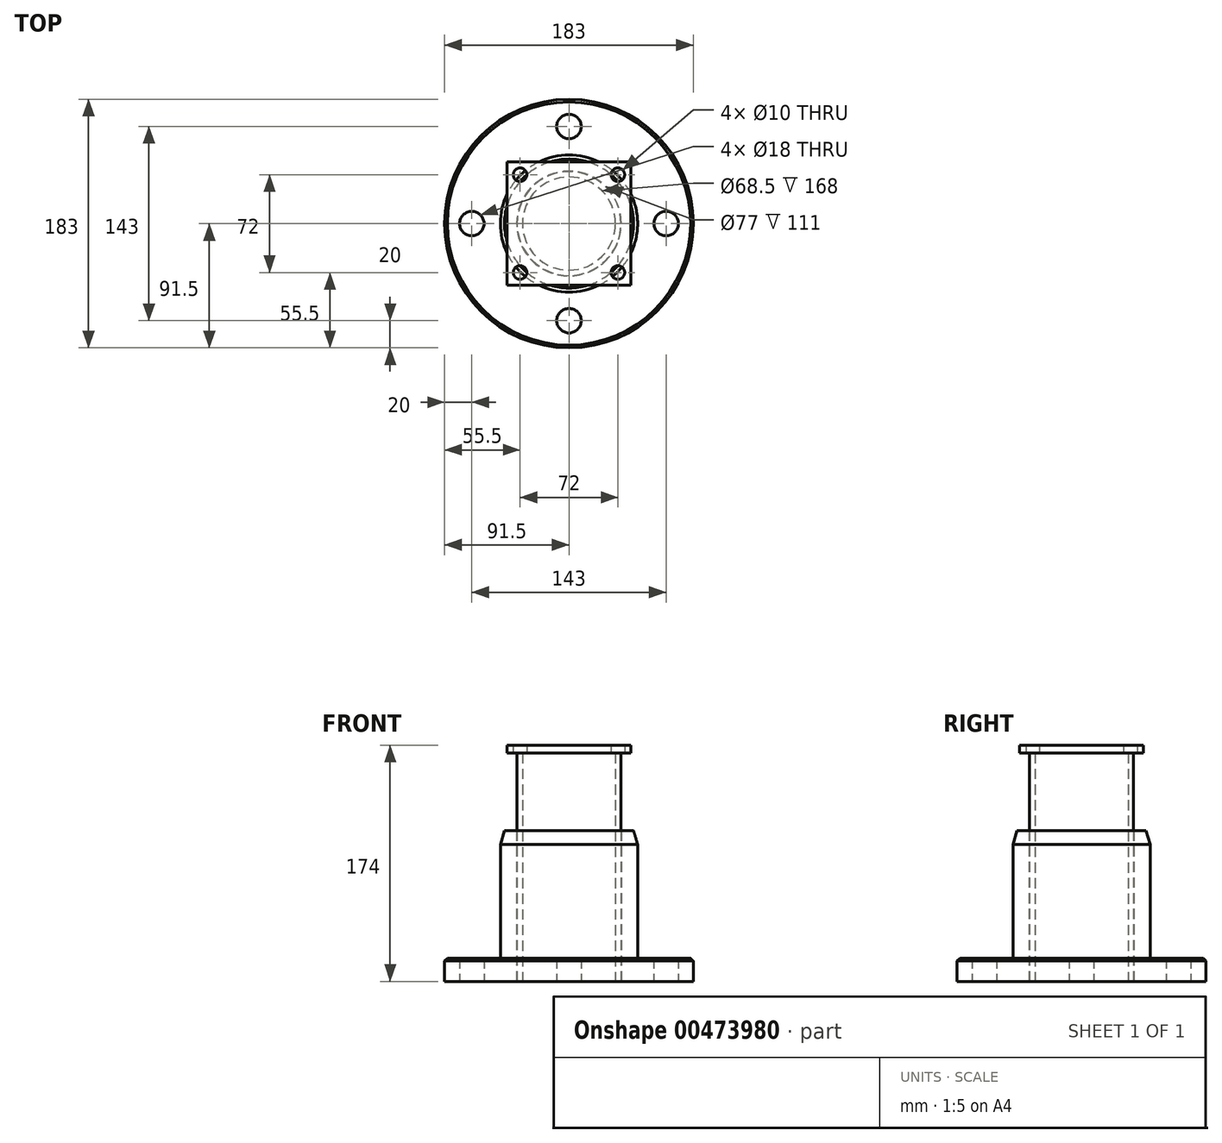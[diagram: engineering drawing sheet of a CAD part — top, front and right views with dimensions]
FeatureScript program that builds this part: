
annotation { "Feature Type Name" : "Feature", "Feature Type Description" : "" }
export const myFeature = defineFeature(function(context is Context, id is Id, definition is map)
    precondition{}
    {
        {
            var Q0;
            Q0=qCreatedBy(makeId("Top.planeOp"),FACE);
            var sketch = newSketch(context, id + "F0", { "sketchPlane" : qUnion([Q0])});
            skCircle(sketch, "E0", {"center": v(0, 0) * mm, "radius": 91.5 * mm});
            skCircle(sketch, "E1", {"center": v(0, 71.5) * mm, "radius": 9 * mm});
            skCircle(sketch, "E2", {"center": v(71.5, 0) * mm, "radius": 9 * mm});
            skCircle(sketch, "E3", {"center": v(-71.5, 0) * mm, "radius": 9 * mm});
            skCircle(sketch, "E4", {"center": v(0, -71.5) * mm, "radius": 9 * mm});
            skCircle(sketch, "E5", {"center": v(0, 0) * mm, "radius": 38.5 * mm});
            skCircle(sketch, "E6", {"center": v(0, 0) * mm, "radius": 71.5 * mm, "construction": true});
            skSolve(sketch);
        }
        {
            var Q0;
            Q0=makeQuery(id+"F0.imprint","IMPRINT",FACE,{"disambiguationData":[TD([[makeQuery(id+"F0.imprint","IMPRINT",EDGE,{"derivedFrom":sQuery(id+"F0.wireOp",EDGE,"E0")}),1.0]])]});
            extrude(context, id + "F1", {"entities" : qUnion([Q0]), "depth" : 17 * mm});
        }
        {
            var Q0;
            Q0=makeQuery(id+"F1.opExtrude","CAP_FACE",FACE,{"disambiguationData":[OSD([sQuery(id+"F0.wireOp",EDGE,"E0"),sQuery(id+"F0.wireOp",EDGE,"E1"),sQuery(id+"F0.wireOp",EDGE,"E2"),sQuery(id+"F0.wireOp",EDGE,"E3"),sQuery(id+"F0.wireOp",EDGE,"E4"),sQuery(id+"F0.wireOp",EDGE,"E5")])],"isStart":false});
            var sketch = newSketch(context, id + "F2", { "sketchPlane" : qUnion([Q0])});
            skCircle(sketch, "E7", {"center": v(0, 0) * mm, "radius": 50.5 * mm});
            skCircle(sketch, "E8", {"center": v(0, 0) * mm, "radius": 38.5 * mm});
            skSolve(sketch);
        }
        {
            var Q0;
            Q0=makeQuery(id+"F2.imprint","IMPRINT",FACE,{"disambiguationData":[TD([[makeQuery(id+"F2.imprint","IMPRINT",EDGE,{"derivedFrom":sQuery(id+"F2.wireOp",EDGE,"E7")}),1.0]])]});
            extrude(context, id + "F3", {"entities" : qUnion([Q0]), "operationType" : NewBodyOperationType.ADD, "depth" : 94 * mm});
        }
        {
            var Q0;
            Q0=makeQuery(id+"F3.opExtrude","CAP_EDGE",EDGE,{"disambiguationData":[OSD([sQuery(id+"F2.wireOp",EDGE,"E7")])],"isStart":false});
            chamfer(context, id + "F4", {"entities" : qUnion([Q0]), "chamferType" : ChamferType.TWO_OFFSETS, "width1" : 3 * mm, "oppositeDirection" : false, "width2" : 10 * mm, "tangentPropagation" : true});
        }
        {
            var Q0;
            Q0=makeQuery(id+"F1.opExtrude","CAP_EDGE",EDGE,{"disambiguationData":[OSD([sQuery(id+"F0.wireOp",EDGE,"E0")])],"isStart":false});
            chamfer(context, id + "F5", {"entities" : qUnion([Q0]), "width" : 2 * mm, "tangentPropagation" : true});
        }
        {
            var Q0;
            Q0=qCreatedBy(makeId("Top.planeOp"),FACE);
            var sketch = newSketch(context, id + "F6", { "sketchPlane" : qUnion([Q0])});
            skCircle(sketch, "E9", {"center": v(0, 0) * mm, "radius": 38.25 * mm});
            skCircle(sketch, "E10", {"center": v(0, 0) * mm, "radius": 34.25 * mm});
            skSolve(sketch);
        }
        {
            var Q0;
            Q0=makeQuery(id+"F6.imprint","IMPRINT",FACE,{"disambiguationData":[TD([[makeQuery(id+"F6.imprint","IMPRINT",EDGE,{"derivedFrom":sQuery(id+"F6.wireOp",EDGE,"E9")}),1.0]])]});
            extrude(context, id + "F7", {"entities" : qUnion([Q0]), "depth" : 168 * mm});
        }
        {
            var Q0;
            Q0=makeQuery(id+"F7.opExtrude","CAP_FACE",FACE,{"disambiguationData":[OSD([sQuery(id+"F6.wireOp",EDGE,"E9"),sQuery(id+"F6.wireOp",EDGE,"E10")])],"isStart":false});
            var sketch = newSketch(context, id + "F8", { "sketchPlane" : qUnion([Q0])});
            skLineSegment(sketch, "E11.bottom", {"start": v(-45.5, 45.5) * mm, "end": v(45.5, 45.5) * mm});
            skLineSegment(sketch, "E11.top", {"start": v(-45.5, -45.5) * mm, "end": v(45.5, -45.5) * mm});
            skLineSegment(sketch, "E11.left", {"start": v(-45.5, 45.5) * mm, "end": v(-45.5, -45.5) * mm});
            skLineSegment(sketch, "E11.right", {"start": v(45.5, 45.5) * mm, "end": v(45.5, -45.5) * mm});
            skCircle(sketch, "E12", {"center": v(-36, 36) * mm, "radius": 5 * mm});
            skCircle(sketch, "E13.MirrorC", {"center": v(36, 36) * mm, "radius": 5 * mm});
            skCircle(sketch, "E14.MirrorC", {"center": v(36, -36) * mm, "radius": 5 * mm});
            skCircle(sketch, "E15.MirrorC", {"center": v(-36, -36) * mm, "radius": 5 * mm});
            skSolve(sketch);
        }
        {
            var Q0;
            Q0 = qSketchRegion(id + "F8", true);
            extrude(context, id + "F9", {"entities" : qUnion([Q0]), "operationType" : NewBodyOperationType.ADD, "depth" : 6 * mm});
        }
    });
